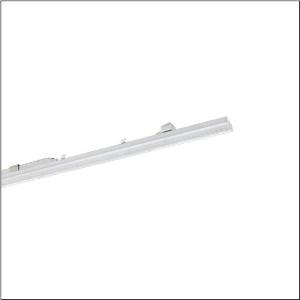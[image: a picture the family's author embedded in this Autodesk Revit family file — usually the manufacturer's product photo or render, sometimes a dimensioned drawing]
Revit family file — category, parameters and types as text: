
# Revit family: tl_l_5wd7a7h0a2b5
name_source: partatom
category: Lighting Fixtures
units: mm (PartAtom-declared; Revit-internal decimal feet)

## family parameters
Cut with Voids When Loaded = No
Host = Face
Light Source = No
Part Type = Normal
Room Calculation Point = No
Round Connector Dimension = Use Diameter
Shared = No

## types (1)
- --- (1 x LED, 790 lm, 4.5 W, 3000K)
    Apparent Load = 5 VA
    CIE Flux Codes = 49 84 98 100 100
    Color Rendering = 80
    Color Temperature = 3000K
    Default Elevation = 1800 mm
    Description = TL L, luminaire insert, of sheet steel, galvanised, coil coated, white, length: 1.500mm, width: 66mm, height: 67mm, LED rated luminous flux: 5.000lm, light colour: 830, control gear: emergency light, with terminal, 3-pole, mains connection: 230..240V, AC, 50/60Hz, rated input power: 36W, primary optical cover: cover, of PMMA, light emission: direct distribution, protection rating (complete): as luminaire, insulation class (complete): insulation class I (protective earthing), certification: CE, impact resistance: IK06, permissible ambient temperature for indoor applications: +5..+35°C, packaging unit: 1 piece
    Height = 120 mm
    Lamp = 1 x LED
    Lamp Light Flux = 790 lm
    Lamp Power = 4.5 W
    Lamp count = 1
    Length = 1690 mm
    Luminous efficacy = 176 lm/W
    Manufacturer = Siteco
    ModVariant = No
    Model = 5WD7A7H0A2B5
    Mounting Place = Ceiling
    Mounting Type = Pendant
    Number of Poles = 1
    OnlyDefault = Yes
    Power Factor = 1
    Product Name = TL L
    Product group = luminaire insert
    ProductGroupID = 901
    Protection Class = Protection class I
    Protection Degree = Degree of protection
    RLX_Detail_Level = 1
    RLX_Emergency_Light_Flux = 0 lm
    RLX_Emergency_Type = 0
    RLX_Emergency_Type_DB = No
    RlxData = <blob elided: 17541 chars, md5=f9c40a9e>
    Socket = socket
    Standby Power = 0 W
    System Light Flux = 790 lm
    System Power = 5 W
    Type Comments = : emergency light operation: 3 h
    Type Image = l_1294382.jpg
    URL = http://relux.com
    VarID = @adj_030885
    Voltage = 0 V
    Weight = 0.00 kg
    Width = 208 mm

## geometry (parser evidence)
native form markers: Blend x4, Sweep x10
no freeform markers — native parametric forms only
